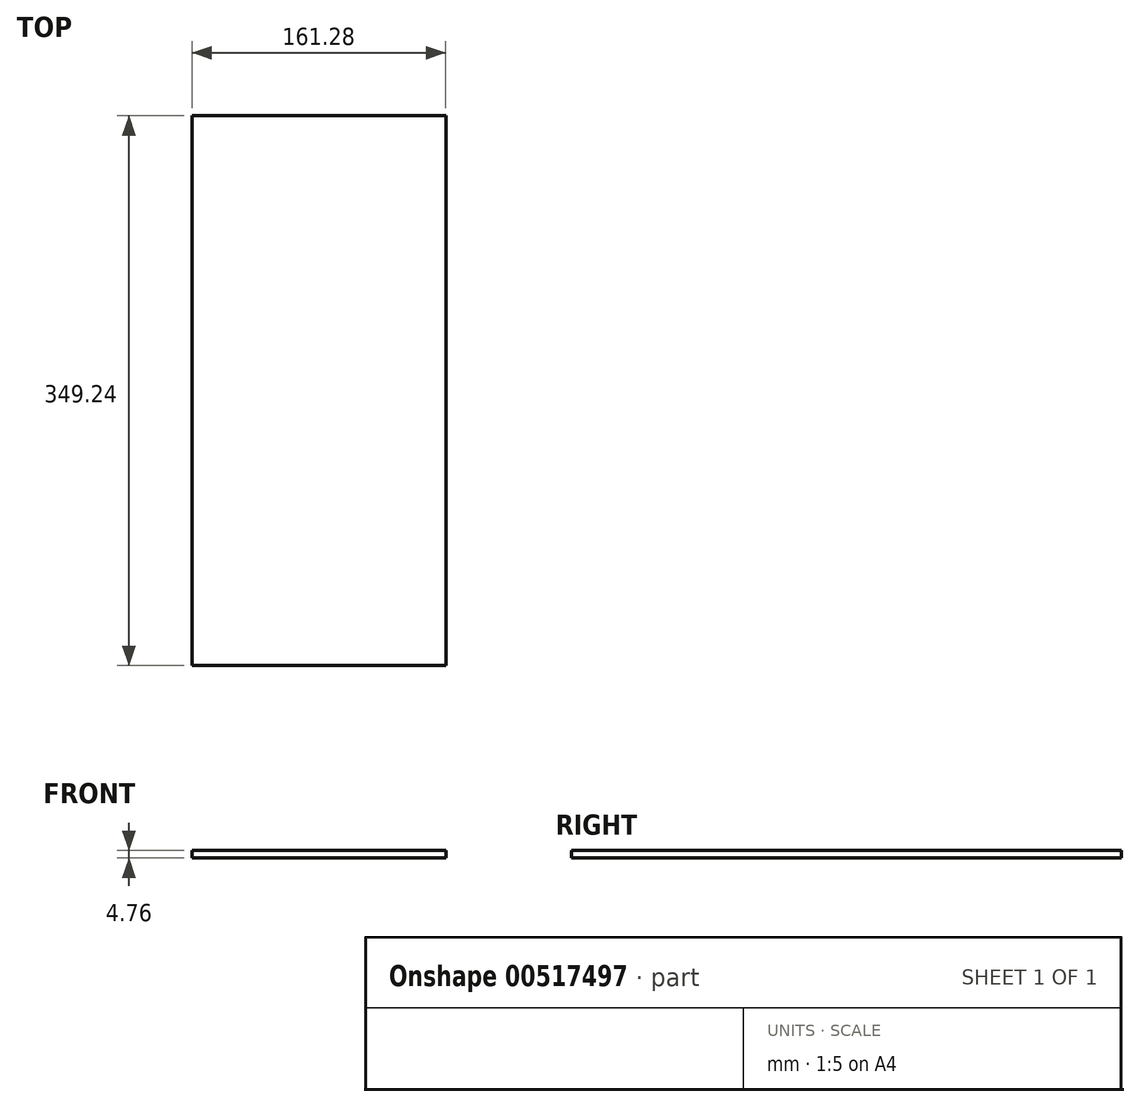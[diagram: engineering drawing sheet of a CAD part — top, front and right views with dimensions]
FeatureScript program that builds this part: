
annotation { "Feature Type Name" : "Feature", "Feature Type Description" : "" }
export const myFeature = defineFeature(function(context is Context, id is Id, definition is map)
    precondition{}
    {
        {
            var Q0;
            Q0=qCreatedBy(makeId("Top.planeOp"),FACE);
            var sketch = newSketch(context, id + "F0", { "sketchPlane" : qUnion([Q0])});
            skLineSegment(sketch, "E0.bottom", {"start": v(80.65, -174.62) * mm, "end": v(-80.65, -174.62) * mm});
            skLineSegment(sketch, "E0.top", {"start": v(80.65, 174.63) * mm, "end": v(-80.64, 174.63) * mm});
            skLineSegment(sketch, "E0.left", {"start": v(80.65, -174.62) * mm, "end": v(80.65, 174.63) * mm});
            skLineSegment(sketch, "E0.right", {"start": v(-80.65, -174.62) * mm, "end": v(-80.64, 174.63) * mm});
            skPoint(sketch, "E0.middle", {"position": v(0, 0) * mm});
            skSolve(sketch);
        }
        {
            var Q0;
            Q0=makeQuery(id+"F0.imprint","IMPRINT",FACE,{"disambiguationData":[TD([[makeQuery(id+"F0.imprint","IMPRINT",EDGE,{"derivedFrom":sQuery(id+"F0.wireOp",EDGE,"E0.bottom")}),-1.0]])]});
            extrude(context, id + "F1", {"entities" : qUnion([Q0]), "depth" : 4.76 * mm, "offsetDistance" : 25.4 * mm});
        }
    });
